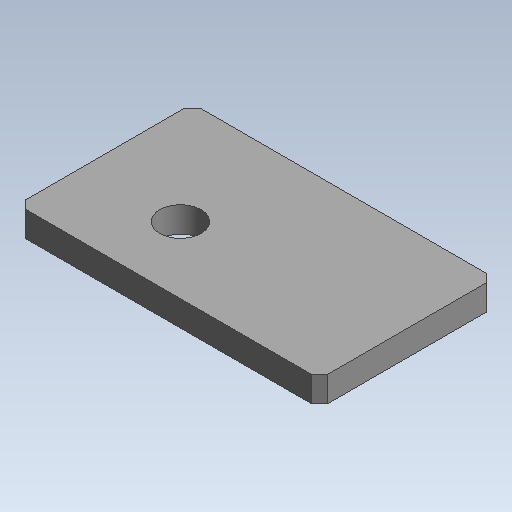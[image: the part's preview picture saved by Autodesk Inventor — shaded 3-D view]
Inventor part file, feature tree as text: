
AUTODESK INVENTOR PART (.ipt)
format: ipt  version: 2020 (Build 240168000, 168)  size: 54,272 bytes
history: native  units: mm (DEFAULTED — no unit token found)
features: chamfer x1
ambient origin geometry x8: Origin, YZ Plane, XZ Plane, XY Plane, X Axis, Y Axis, Z Axis, Center Point
bodies: Solid1 (feature_tree)
feature tree (1):
  chamfer  "Chamfer1"  [1 undecoded]
note: 1 required parameter value undecoded (feature->parameter linkage not recoverable at this tier; creation-order binding heuristic only, values carry confidence <= 0.55)
